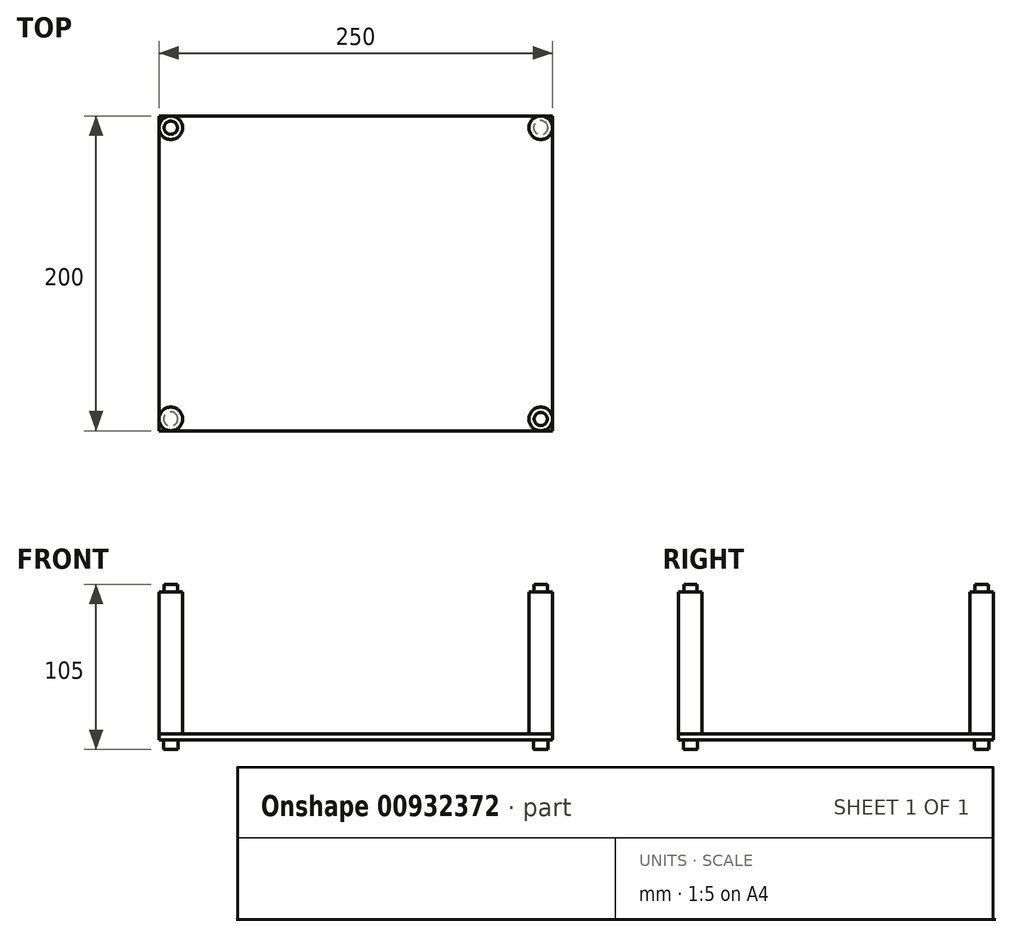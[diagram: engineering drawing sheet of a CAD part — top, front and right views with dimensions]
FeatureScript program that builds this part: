
annotation { "Feature Type Name" : "Feature", "Feature Type Description" : "" }
export const myFeature = defineFeature(function(context is Context, id is Id, definition is map)
    precondition{}
    {
        {
            assignVariable(context, id + "F0", {"name" : "width", "anyValue" : 250});
        }
        {
            assignVariable(context, id + "F1", {"name" : "height", "anyValue" : 100});
        }
        {
            var Q0;
            Q0=qCreatedBy(makeId("Right.planeOp"),FACE);
            var sketch = newSketch(context, id + "F2", { "sketchPlane" : qUnion([Q0])});
            skLineSegment(sketch, "E0", {"start": v(100, 0) * mm, "end": v(-100, 0) * mm});
            skLineSegment(sketch, "E1", {"start": v(100, 10) * mm, "end": v(-100, 10) * mm});
            skLineSegment(sketch, "E2", {"start": v(-100, 10) * mm, "end": v(-100, 0) * mm});
            skLineSegment(sketch, "E3", {"start": v(100, 0) * mm, "end": v(100, 10) * mm});
            skSolve(sketch);
        }
        {
            var Q0;
            Q0=makeQuery(id+"F2.imprint","IMPRINT",FACE,{"disambiguationData":[TD([[makeQuery(id+"F2.imprint","IMPRINT",EDGE,{"derivedFrom":sQuery(id+"F2.wireOp",EDGE,"E0")}),-1.0]])]});
            extrude(context, id + "F3", {"entities" : qUnion([Q0]), "endBound" : BoundingType.SYMMETRIC, "depth" : (getVariable(context, 'width')) * mm, "offsetDistance" : 25 * mm});
        }
        {
            var Q0;
            {var subQ0=sQuery(id+"F2.wireOp",EDGE,"E0");Q0=makeQuery(id+"FtaCGZXW4uEEXou_1.1.FbIlMp8xrE71BWM_1.boolean.opBoolean","MERGE",FACE,{"derivedFrom":[makeQuery(id+"FbIlMp8xrE71BWM_1.boolean.opBoolean","MERGE",FACE,{"derivedFrom":[makeQuery(id+"F3.opExtrude","SWEPT_FACE",FACE,{"disambiguationData":[OSD([subQ0])]}),makeQuery(id+"FbIlMp8xrE71BWM_1.opExtrude","SWEPT_FACE",FACE,{"disambiguationData":[OSD([subQ0])]})]}),makeQuery(id+"FtaCGZXW4uEEXou_1.1.FbIlMp8xrE71BWM_1.opExtrude","SWEPT_FACE",FACE,{"disambiguationData":[OSD([subQ0])]})]});}
            var sketch = newSketch(context, id + "F4", { "sketchPlane" : qUnion([Q0])});
            skCircle(sketch, "E4", {"center": v(-117.5, -92.5) * mm, "radius": 7.5 * mm});
            skCircle(sketch, "E5.MirrorC", {"center": v(117.5, -92.5) * mm, "radius": 7.5 * mm});
            skCircle(sketch, "E6.MirrorC", {"center": v(117.5, 92.5) * mm, "radius": 7.5 * mm});
            skCircle(sketch, "E7.MirrorC", {"center": v(-117.5, 92.5) * mm, "radius": 7.5 * mm});
            skSolve(sketch);
        }
        {
            var Q0;
            Q0=qSketchRegion(id+"F4",true);
            extrude(context, id + "F5", {"entities" : qUnion([Q0]), "operationType" : NewBodyOperationType.ADD, "oppositeDirection" : true, "depth" : (getVariable(context, 'height')) * mm, "offsetDistance" : 25 * mm});
        }
        {
            var Q0;
            {var subQ0=sQuery(id+"F2.wireOp",EDGE,"E0");Q0=makeQuery(id+"F5.boolean.opBoolean","MERGE",FACE,{"derivedFrom":[makeQuery(id+"FtaCGZXW4uEEXou_1.1.FbIlMp8xrE71BWM_1.boolean.opBoolean","MERGE",FACE,{"derivedFrom":[makeQuery(id+"FbIlMp8xrE71BWM_1.boolean.opBoolean","MERGE",FACE,{"derivedFrom":[makeQuery(id+"F3.opExtrude","SWEPT_FACE",FACE,{"disambiguationData":[OSD([subQ0])]}),makeQuery(id+"FbIlMp8xrE71BWM_1.opExtrude","SWEPT_FACE",FACE,{"disambiguationData":[OSD([subQ0])]})]}),makeQuery(id+"FtaCGZXW4uEEXou_1.1.FbIlMp8xrE71BWM_1.opExtrude","SWEPT_FACE",FACE,{"disambiguationData":[OSD([subQ0])]})]}),makeQuery(id+"F5.opExtrude","CAP_FACE",FACE,{"disambiguationData":[OSD([sQuery(id+"F4.wireOp",EDGE,"E4")])],"isStart":true}),makeQuery(id+"F5.opExtrude","CAP_FACE",FACE,{"disambiguationData":[OSD([sQuery(id+"F4.wireOp",EDGE,"PZxf8rwE-Nqhv-zmbJ-LZSK-HnXBbpmZNIQM")])],"isStart":true}),makeQuery(id+"F5.opExtrude","CAP_FACE",FACE,{"disambiguationData":[OSD([sQuery(id+"F4.wireOp",EDGE,"iXyLZq5x-45gI-Opsh-ObeK-aBQ05S0Pxcr3")])],"isStart":true}),makeQuery(id+"F5.opExtrude","CAP_FACE",FACE,{"disambiguationData":[OSD([sQuery(id+"F4.wireOp",EDGE,"hLY0BQU8-ux8d-mXx6-vVSP-pXOVl9mUcjdP")])],"isStart":true})]});}
            var sketch = newSketch(context, id + "F6", { "sketchPlane" : qUnion([Q0])});
            skCircle(sketch, "E8.0", {"center": v(-117.5, -92.5) * mm, "radius": 4.5 * mm});
            skCircle(sketch, "E9.MirrorC", {"center": v(117.5, -92.5) * mm, "radius": 4.5 * mm});
            skCircle(sketch, "E10.MirrorC", {"center": v(-117.5, 92.5) * mm, "radius": 4.5 * mm});
            skCircle(sketch, "E11.MirrorC", {"center": v(117.5, 92.5) * mm, "radius": 4.5 * mm});
            skSolve(sketch);
        }
        {
            var Q0;
            Q0=makeQuery(id+"F6.imprint","IMPRINT",FACE,{"disambiguationData":[TD([[makeQuery(id+"F6.imprint","IMPRINT",EDGE,{"derivedFrom":sQuery(id+"F6.wireOp",EDGE,"E10.MirrorC")}),-1.0]])]});
            var Q1;
            Q1=makeQuery(id+"F6.imprint","IMPRINT",FACE,{"disambiguationData":[TD([[makeQuery(id+"F6.imprint","IMPRINT",EDGE,{"derivedFrom":sQuery(id+"F6.wireOp",EDGE,"E8.0")}),1.0]])]});
            var Q2;
            Q2=makeQuery(id+"F6.imprint","IMPRINT",FACE,{"disambiguationData":[TD([[makeQuery(id+"F6.imprint","IMPRINT",EDGE,{"derivedFrom":sQuery(id+"F6.wireOp",EDGE,"E11.MirrorC")}),1.0]])]});
            var Q3;
            Q3=makeQuery(id+"F6.imprint","IMPRINT",FACE,{"disambiguationData":[TD([[makeQuery(id+"F6.imprint","IMPRINT",EDGE,{"derivedFrom":sQuery(id+"F6.wireOp",EDGE,"E9.MirrorC")}),-1.0]])]});
            extrude(context, id + "F7", {"entities" : qUnion([Q0, Q1, Q2, Q3]), "operationType" : NewBodyOperationType.REMOVE, "oppositeDirection" : true, "depth" : 6 * mm, "offsetDistance" : 25 * mm});
        }
        {
            var Q0;
            Q0=makeQuery(id+"F5.opExtrude","CAP_FACE",FACE,{"disambiguationData":[OSD([sQuery(id+"F4.wireOp",EDGE,"E4")])],"isStart":false});
            var sketch = newSketch(context, id + "F8", { "sketchPlane" : qUnion([Q0])});
            skCircle(sketch, "E12.0", {"center": v(-117.5, 92.5) * mm, "radius": 4.2 * mm});
            skCircle(sketch, "E13.MirrorC", {"center": v(117.5, 92.5) * mm, "radius": 4.2 * mm});
            skCircle(sketch, "E14.MirrorC", {"center": v(-117.5, -92.5) * mm, "radius": 4.2 * mm});
            skCircle(sketch, "E15.MirrorC", {"center": v(117.5, -92.5) * mm, "radius": 4.2 * mm});
            skSolve(sketch);
        }
        {
            var Q0;
            Q0=makeQuery(id+"F8.imprint","IMPRINT",FACE,{"disambiguationData":[TD([[makeQuery(id+"F8.imprint","IMPRINT",EDGE,{"derivedFrom":sQuery(id+"F8.wireOp",EDGE,"E12.0")}),1.0]])]});
            var Q1;
            Q1=makeQuery(id+"F8.imprint","IMPRINT",FACE,{"disambiguationData":[TD([[makeQuery(id+"F8.imprint","IMPRINT",EDGE,{"derivedFrom":sQuery(id+"F8.wireOp",EDGE,"E13.MirrorC")}),-1.0]])]});
            var Q2;
            Q2=makeQuery(id+"F8.imprint","IMPRINT",FACE,{"disambiguationData":[TD([[makeQuery(id+"F8.imprint","IMPRINT",EDGE,{"derivedFrom":sQuery(id+"F8.wireOp",EDGE,"E15.MirrorC")}),1.0]])]});
            var Q3;
            Q3=makeQuery(id+"F8.imprint","IMPRINT",FACE,{"disambiguationData":[TD([[makeQuery(id+"F8.imprint","IMPRINT",EDGE,{"derivedFrom":sQuery(id+"F8.wireOp",EDGE,"E14.MirrorC")}),-1.0]])]});
            extrude(context, id + "F9", {"entities" : qUnion([Q0, Q1, Q2, Q3]), "operationType" : NewBodyOperationType.ADD, "depth" : 5 * mm, "offsetDistance" : 25 * mm});
        }
    });
